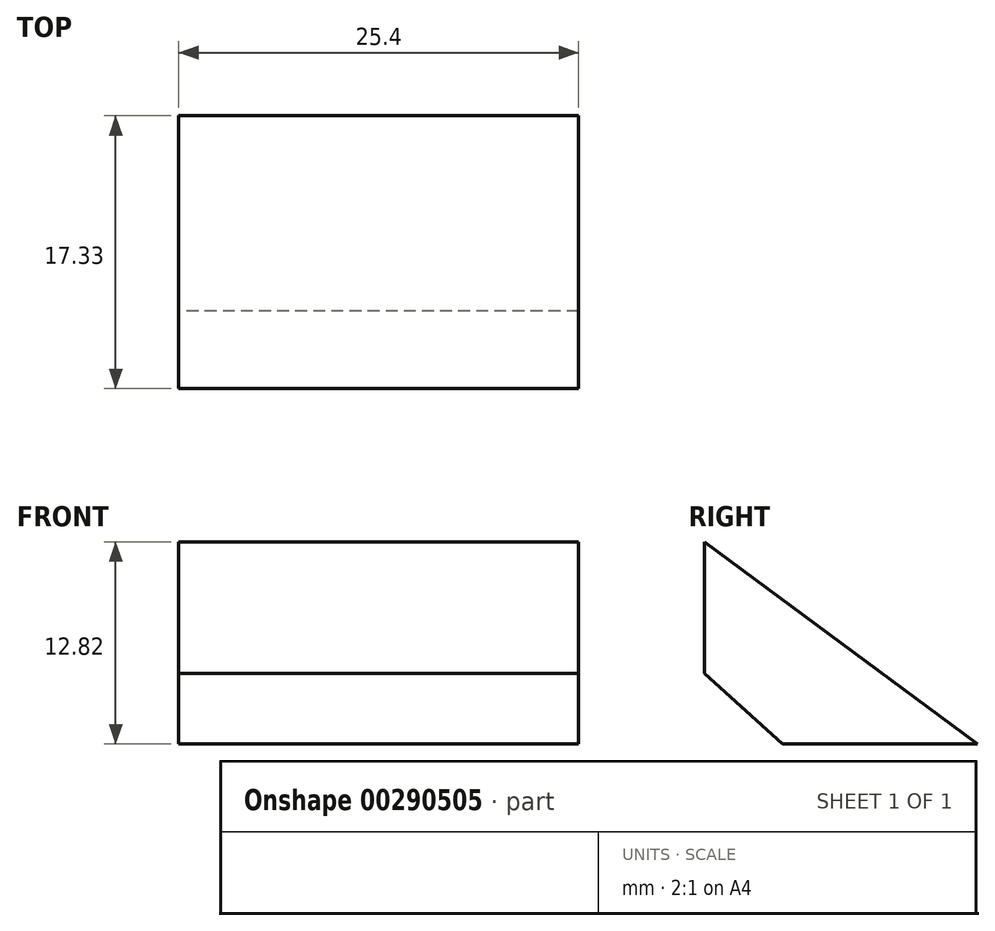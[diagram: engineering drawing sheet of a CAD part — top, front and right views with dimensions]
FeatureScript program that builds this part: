
annotation { "Feature Type Name" : "Feature", "Feature Type Description" : "" }
export const myFeature = defineFeature(function(context is Context, id is Id, definition is map)
    precondition{}
    {
        {
            var Q0;
            Q0=qCreatedBy(makeId("Right.planeOp"),FACE);
            var sketch = newSketch(context, id + "F0", { "sketchPlane" : qUnion([Q0])});
            skLineSegment(sketch, "E0", {"start": v(14.2, 12.82) * mm, "end": v(14.2, 4.48) * mm});
            skLineSegment(sketch, "E1", {"start": v(14.2, 4.48) * mm, "end": v(19.13, 0) * mm});
            skLineSegment(sketch, "E2", {"start": v(19.13, 0) * mm, "end": v(31.53, 0) * mm});
            skLineSegment(sketch, "E3", {"start": v(31.53, 0) * mm, "end": v(14.2, 12.82) * mm});
            skSolve(sketch);
        }
        {
            var Q0;
            Q0=makeQuery(id+"F0.imprint","IMPRINT",FACE,{"disambiguationData":[TD([[makeQuery(id+"F0.imprint","IMPRINT",EDGE,{"derivedFrom":sQuery(id+"F0.wireOp",EDGE,"E0")}),1.0]])]});
            extrude(context, id + "F1", {"entities" : qUnion([Q0]), "depth" : 25.4 * mm});
        }
    });
